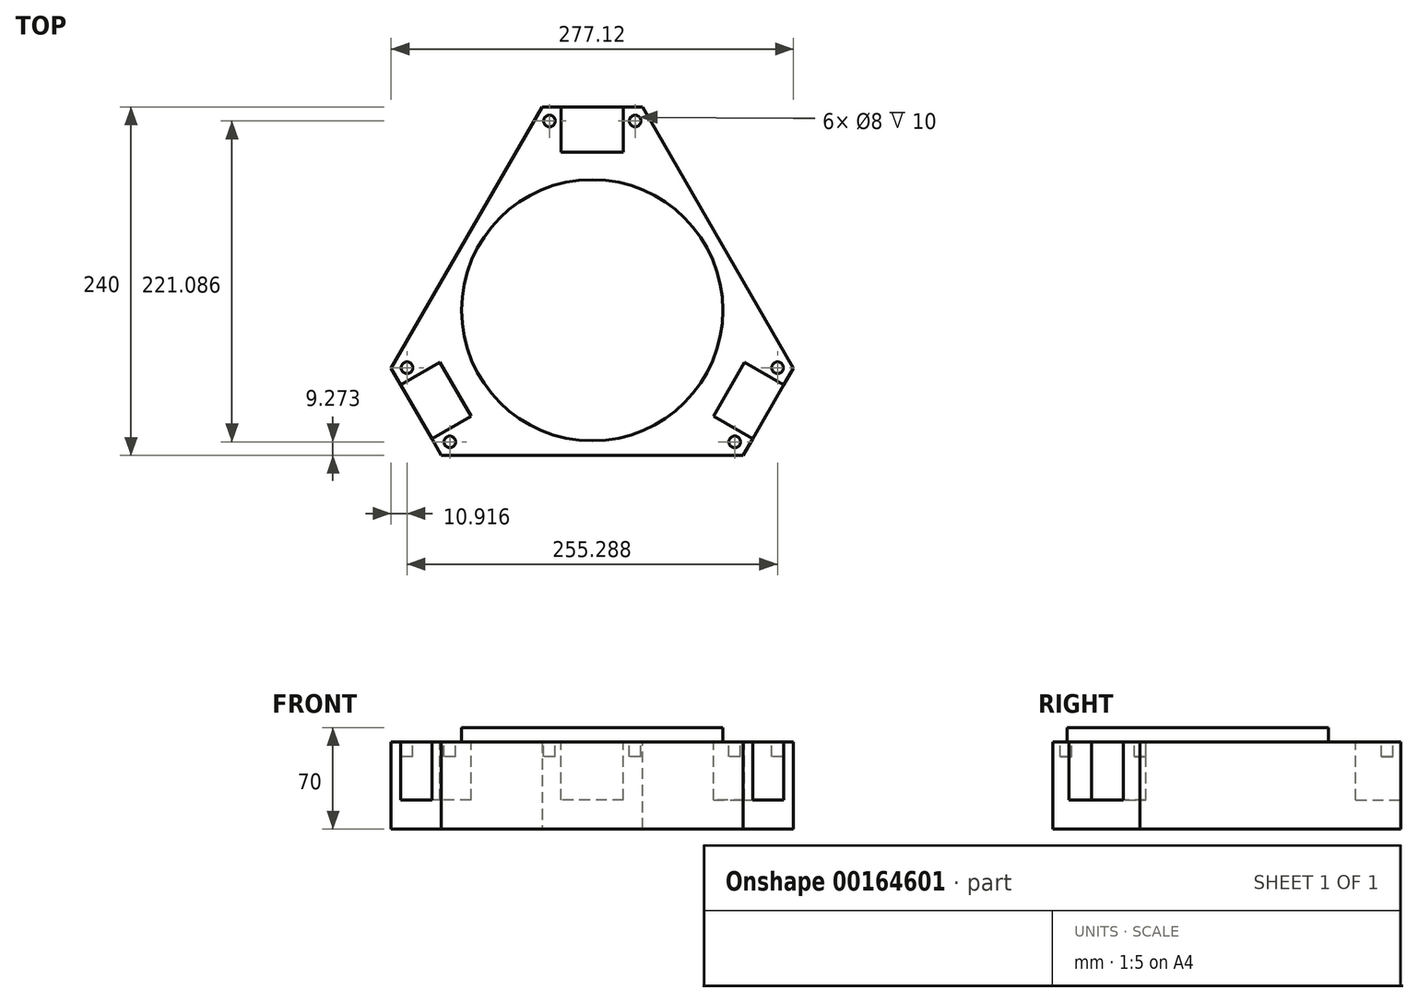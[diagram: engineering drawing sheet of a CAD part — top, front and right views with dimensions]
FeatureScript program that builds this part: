
annotation { "Feature Type Name" : "Feature", "Feature Type Description" : "" }
export const myFeature = defineFeature(function(context is Context, id is Id, definition is map)
    precondition{}
    {
        {
            var Q0;
            Q0=qCreatedBy(makeId("Top.planeOp"),FACE);
            var sketch = newSketch(context, id + "F0", { "sketchPlane" : qUnion([Q0])});
            skCircle(sketch, "E0.cCircle", {"center": v(0, 0) * mm, "radius": 100 * mm, "construction": true});
            skLineSegment(sketch, "E0.0", {"start": v(173.2, -100) * mm, "end": v(-173.2, -100) * mm});
            skLineSegment(sketch, "E0.1", {"start": v(-173.2, -100) * mm, "end": v(0, 200) * mm});
            skLineSegment(sketch, "E0.2", {"start": v(0, 200) * mm, "end": v(173.2, -100) * mm});
            skPoint(sketch, "E0.0.midPoint", {"position": v(0, -100) * mm});
            skSolve(sketch);
        }
        {
            var Q0;
            Q0 = qSketchRegion(id + "F0", true);
            extrude(context, id + "F1", {"entities" : qUnion([Q0]), "depth" : 60 * mm});
        }
        {
            var Q0;
            Q0=makeQuery(id+"F1.opExtrude","SWEPT_EDGE",EDGE,{"disambiguationData":[OSD([sQuery(id+"F0.wireOp",EDGE,"E0.0"),sQuery(id+"F0.wireOp",EDGE,"E0.1")])]});
            var Q1;
            Q1=makeQuery(id+"F1.opExtrude","SWEPT_EDGE",EDGE,{"disambiguationData":[OSD([sQuery(id+"F0.wireOp",EDGE,"E0.0"),sQuery(id+"F0.wireOp",EDGE,"E0.2")])]});
            var Q2;
            Q2=makeQuery(id+"F1.opExtrude","SWEPT_EDGE",EDGE,{"disambiguationData":[OSD([sQuery(id+"F0.wireOp",EDGE,"E0.1"),sQuery(id+"F0.wireOp",EDGE,"E0.2")])]});
            chamfer(context, id + "F2", {"entities" : qUnion([Q0, Q1, Q2]), "width" : 40 * mm, "tangentPropagation" : true});
        }
        {
            var Q0;
            Q0=makeQuery(id+"F1.opExtrude","CAP_FACE",FACE,{"disambiguationData":[OSD([sQuery(id+"F0.wireOp",EDGE,"E0.0"),sQuery(id+"F0.wireOp",EDGE,"E0.1"),sQuery(id+"F0.wireOp",EDGE,"E0.2")])],"isStart":false});
            var sketch = newSketch(context, id + "F3", { "sketchPlane" : qUnion([Q0])});
            skCircle(sketch, "E1", {"center": v(0, 0) * mm, "radius": 90 * mm});
            skSolve(sketch);
        }
        {
            var Q0;
            Q0 = qSketchRegion(id + "F3", true);
            extrude(context, id + "F4", {"entities" : qUnion([Q0]), "operationType" : NewBodyOperationType.ADD, "depth" : 10 * mm});
        }
        {
            var Q0;
            Q0=makeQuery(id+"F1.opExtrude","CAP_FACE",FACE,{"disambiguationData":[OSD([sQuery(id+"F0.wireOp",EDGE,"E0.0"),sQuery(id+"F0.wireOp",EDGE,"E0.1"),sQuery(id+"F0.wireOp",EDGE,"E0.2")])],"isStart":false});
            var sketch = newSketch(context, id + "F5", { "sketchPlane" : qUnion([Q0])});
            skLineSegment(sketch, "E2.bottom", {"start": v(-21.5, 108.86) * mm, "end": v(21.5, 108.86) * mm});
            skLineSegment(sketch, "E2.top", {"start": v(-21.5, 151.86) * mm, "end": v(21.5, 151.86) * mm});
            skLineSegment(sketch, "E2.left", {"start": v(-21.5, 108.86) * mm, "end": v(-21.5, 151.86) * mm});
            skLineSegment(sketch, "E2.right", {"start": v(21.5, 108.86) * mm, "end": v(21.5, 151.86) * mm});
            skPoint(sketch, "E2.middle", {"position": v(0, 130.36) * mm});
            skLineSegment(sketch, "E3.1.0", {"start": v(-83.52, -73.05) * mm, "end": v(-105.02, -35.8) * mm});
            skPoint(sketch, "E3.1.1", {"position": v(-112.9, -65.18) * mm});
            skLineSegment(sketch, "E3.1.2", {"start": v(-105.02, -35.8) * mm, "end": v(-142.26, -57.3) * mm});
            skLineSegment(sketch, "E3.1.3", {"start": v(-83.52, -73.05) * mm, "end": v(-120.76, -94.55) * mm});
            skLineSegment(sketch, "E3.1.4", {"start": v(-120.76, -94.55) * mm, "end": v(-142.26, -57.3) * mm});
            skLineSegment(sketch, "E3.2.0", {"start": v(105.02, -35.8) * mm, "end": v(83.52, -73.05) * mm});
            skPoint(sketch, "E3.2.1", {"position": v(112.9, -65.18) * mm});
            skLineSegment(sketch, "E3.2.2", {"start": v(83.52, -73.05) * mm, "end": v(120.76, -94.55) * mm});
            skLineSegment(sketch, "E3.2.3", {"start": v(105.02, -35.8) * mm, "end": v(142.26, -57.3) * mm});
            skLineSegment(sketch, "E3.2.4", {"start": v(142.26, -57.3) * mm, "end": v(120.76, -94.55) * mm});
            skPoint(sketch, "E3.center", {"position": v(0, 0) * mm});
            skSolve(sketch);
        }
        {
            var Q0;
            Q0 = qSketchRegion(id + "F5", true);
            extrude(context, id + "F6", {"entities" : qUnion([Q0]), "operationType" : NewBodyOperationType.REMOVE, "oppositeDirection" : true, "depth" : 40 * mm});
        }
        {
            var Q0;
            Q0=makeQuery(id+"F1.opExtrude","CAP_FACE",FACE,{"disambiguationData":[OSD([sQuery(id+"F0.wireOp",EDGE,"E0.0"),sQuery(id+"F0.wireOp",EDGE,"E0.1"),sQuery(id+"F0.wireOp",EDGE,"E0.2")])],"isStart":false});
            var sketch = newSketch(context, id + "F7", { "sketchPlane" : qUnion([Q0])});
            skCircle(sketch, "E4", {"center": v(-29.5, 130.36) * mm, "radius": 4 * mm});
            skPoint(sketch, "E4.centerSnap0", {"position": v(-21.5, 130.36) * mm});
            skCircle(sketch, "E5", {"center": v(29.5, 130.36) * mm, "radius": 4 * mm});
            skPoint(sketch, "E5.centerSnap0", {"position": v(21.5, 130.36) * mm});
            skCircle(sketch, "E6.1.0", {"center": v(-98.14, -90.73) * mm, "radius": 4 * mm});
            skCircle(sketch, "E6.1.1", {"center": v(-127.64, -39.63) * mm, "radius": 4 * mm});
            skCircle(sketch, "E6.2.0", {"center": v(127.64, -39.63) * mm, "radius": 4 * mm});
            skCircle(sketch, "E6.2.1", {"center": v(98.14, -90.73) * mm, "radius": 4 * mm});
            skPoint(sketch, "E6.center", {"position": v(0, 0) * mm});
            skSolve(sketch);
        }
        {
            var Q0;
            Q0 = qSketchRegion(id + "F7", true);
            extrude(context, id + "F8", {"entities" : qUnion([Q0]), "operationType" : NewBodyOperationType.REMOVE, "oppositeDirection" : true, "depth" : 10 * mm});
        }
    });
